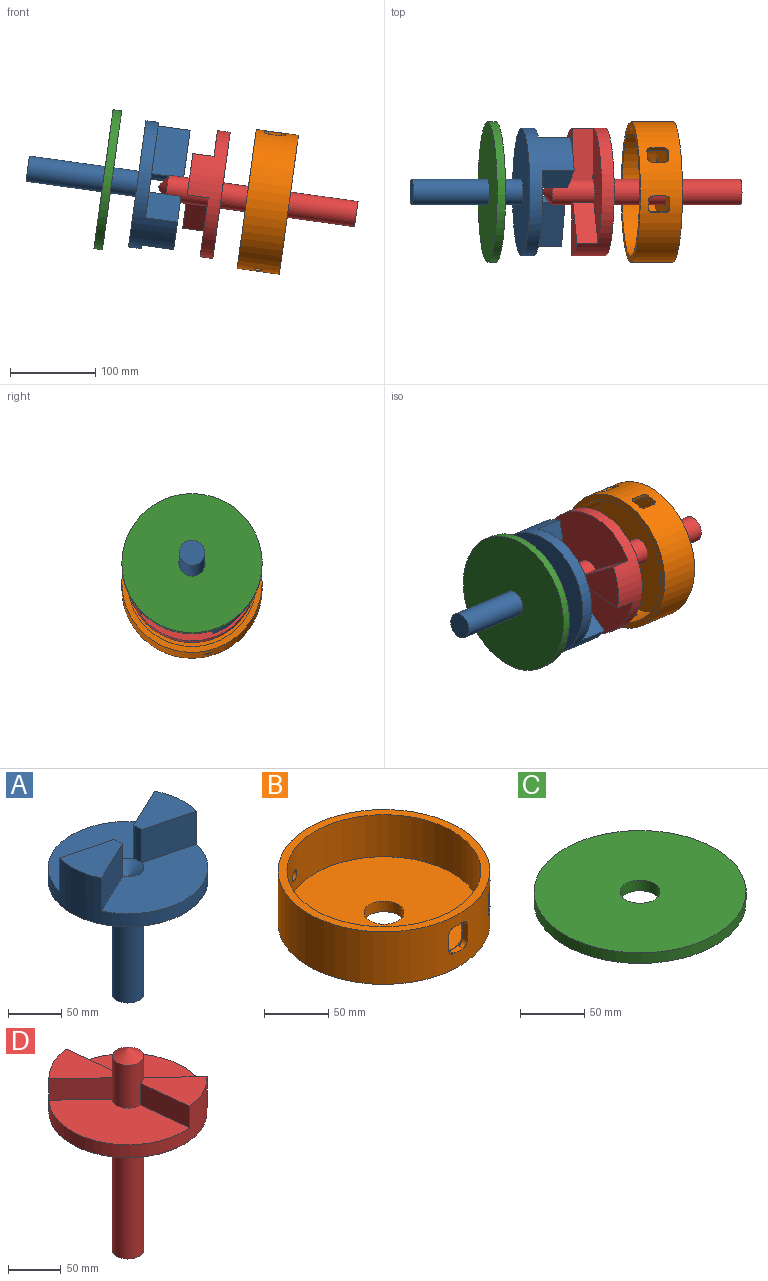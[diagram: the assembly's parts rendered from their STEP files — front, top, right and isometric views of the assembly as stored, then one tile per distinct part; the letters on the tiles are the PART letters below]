
ASSEMBLY  parts=4 mates=3
PART A: 14 faces, bbox 150x150x183 mm
  f0: plane 140.27x71.28mm, normal (0,0,1), area 6597.3mm2, adj f2,f6,f7,f9
  f1: plane 61.48x51.05mm, normal (0,0,1), area 1885mm2, adj f2,f4,f6,f9
  f2: cylinder r=75mm len=150mm, axis (0,0,-1), area 11047.9mm2, adj f0,f1,f3,f4,f5,f6,f7,f8
  f3: plane 61.48x51.05mm, normal (0,0,1), area 1885mm2, adj f2,f5,f7,f9
  f4: plane 54.09x38mm, normal (0.43,-0.9,0), area 2280mm2, adj f1,f2,f8,f9
  f5: plane 58.13x38mm, normal (-0.25,-0.97,0), area 2280mm2, adj f2,f3,f8,f9
  f6: plane 58.13x38mm, normal (0.25,0.97,0), area 2280mm2, adj f0,f1,f2,f9
  f7: plane 54.09x38mm, normal (-0.43,0.9,0), area 2280mm2, adj f0,f2,f3,f9
  f8: plane 140.27x71.28mm, normal (0,0,1), area 6597.3mm2, adj f2,f4,f5,f9
  f9: cylinder r=15mm len=38mm, axis (0,0,1), area 795.9mm2, adj f0,f1,f3,f4,f5,f6,f7,f8
  f10: plane 150x150mm, normal (0,0,-1), area 16964.6mm2, adj f2,f11
  f11: cylinder r=15mm len=130mm, axis (0,0,1), area 12252.2mm2, adj f10,f12
  f12: plane 30x30mm, normal (0,0,-1), area 706.9mm2, adj f11
  f13: cone r=15mm half-angle=56.3deg, axis (0,0,1), area 849.5mm2, adj f9
PART B: 40 faces, bbox 165x165x50 mm
  f0: cylinder r=75.5mm len=151mm, axis (0,0,-1), area 17629.2mm2, adj f2,f3,f14,f15,f16,f17,f18,f19
  f1: cylinder r=82.5mm len=165mm, axis (0,0,-1), area 24886mm2, adj f2,f4,f6,f7,f8,f9,f10,f11
  f2: plane 165x165mm, normal (0,0,1), area 3474.6mm2, adj f0,f1
  f3: plane 151x151mm, normal (0,0,1), area 17153.1mm2, adj f0,f5
  f4: plane 165x165mm, normal (0,0,-1), area 20627.7mm2, adj f1,f5
  f5: cylinder r=15.5mm len=31mm, axis (0,0,-1), area 973.9mm2, adj f3,f4
  f6: plane 10x5.19mm, normal (0,0,-1), area 50mm2, adj f1,f10,f13,f14
  f7: plane 15x5.34mm, normal (1,0,0), area 80.1mm2, adj f1,f10,f11,f18
  f8: plane 10x5.19mm, normal (0,0,1), area 50mm2, adj f1,f11,f12,f21
  f9: plane 15x5.31mm, normal (-1,0,0), area 79.7mm2, adj f1,f12,f13,f17
  f10: cylinder r=5mm len=5.82mm, axis (0,-1,0), area 40.8mm2, adj f1,f6,f7,f16
  f11: cylinder r=5mm len=5.82mm, axis (0,1,0), area 40.8mm2, adj f1,f7,f8,f20
  f12: cylinder r=5mm len=5.74mm, axis (0,-1,0), area 40.7mm2, adj f1,f8,f9,f19
  f13: cylinder r=5mm len=5.74mm, axis (0,1,0), area 40.7mm2, adj f1,f6,f9,f15
  f14: torus R=77.5mm, axis (0,0,-1), area 30.9mm2, adj f0,f6,f15,f16
  f15: bspline ~8.33x7.39mm, area 26.8mm2, adj f0,f13,f14,f17
  f16: bspline ~8.55x8.33mm, area 26.7mm2, adj f0,f10,f14,f18
  f17: cylinder r=2mm len=15mm, axis (0,0,-1), area 42.6mm2, adj f0,f9,f15,f19
  f18: cylinder r=2mm len=15mm, axis (0,0,-1), area 42.3mm2, adj f0,f7,f16,f20
  f19: bspline ~8.55x7.2mm, area 26.8mm2, adj f0,f12,f17,f21
  f20: bspline ~8.55x8.33mm, area 26.7mm2, adj f0,f11,f18,f21
  f21: torus R=77.5mm, axis (0,0,-1), area 30.9mm2, adj f0,f8,f19,f20
  f22: plane 15x3.88mm, normal (0.71,0.71,0), area 82.2mm2, adj f1,f26,f29,f30
  f23: plane 10.99x10.24mm, normal (0,0,-1), area 50.1mm2, adj f1,f26,f27,f33
  f24: plane 15x3.67mm, normal (-0.71,-0.71,0), area 77.8mm2, adj f1,f27,f28,f37
  f25: plane 10.99x10.24mm, normal (0,0,1), area 50.1mm2, adj f1,f28,f29,f34
  f26: cylinder r=5mm len=7.92mm, axis (-0.71,0.71,0), area 41.6mm2, adj f1,f22,f23,f31
  f27: cylinder r=5mm len=7.35mm, axis (0.71,-0.71,0), area 40.1mm2, adj f1,f23,f24,f35
  f28: cylinder r=5mm len=7.35mm, axis (-0.71,0.71,0), area 40.1mm2, adj f1,f24,f25,f36
  f29: cylinder r=5mm len=7.92mm, axis (0.71,-0.71,0), area 41.6mm2, adj f1,f22,f25,f32
  f30: cylinder r=2mm len=15mm, axis (0,0,-1), area 40.8mm2, adj f0,f22,f31,f32
  f31: bspline ~8.54x7.77mm, area 26.3mm2, adj f0,f26,f30,f33
  f32: bspline ~7.77x7.39mm, area 26.3mm2, adj f0,f29,f30,f34
  f33: torus R=77.5mm, axis (0,0,1), area 31mm2, adj f0,f23,f31,f35
  f34: torus R=77.5mm, axis (0,0,1), area 31mm2, adj f0,f25,f32,f36
  f35: bspline ~8.56x7.28mm, area 27.2mm2, adj f0,f27,f33,f37
  f36: bspline ~8.56x6.69mm, area 27.2mm2, adj f0,f28,f34,f37
  f37: cylinder r=2mm len=15mm, axis (0,0,-1), area 44.1mm2, adj f0,f24,f35,f36
  f38: cone r=5mm half-angle=5deg, axis (0.38,-0.92,0), area 75mm2, adj f1,f39
  f39: cone r=5mm half-angle=5deg, axis (-0.38,0.92,0), area 138.4mm2, adj f0,f38
PART C: 4 faces, bbox 165x165x10 mm
  f0: cylinder r=82.5mm len=165mm, axis (0,0,-1), area 5183.6mm2, adj f1,f2
  f1: plane 165x165mm, normal (0,0,1), area 20627.7mm2, adj f0,f3
  f2: plane 165x165mm, normal (0,0,-1), area 20627.7mm2, adj f0,f3
  f3: cylinder r=15.5mm len=31mm, axis (0,0,1), area 973.9mm2, adj f1,f2
PART D: 15 faces, bbox 150x150x235 mm
  f0: cylinder r=15mm len=160mm, axis (0,0,-1), area 15079.6mm2, adj f3,f12
  f1: plane 126.89x83.13mm, normal (0,0,1), area 6597.3mm2, adj f6,f8,f10,f11
  f2: plane 126.89x83.13mm, normal (0,0,1), area 6597.3mm2, adj f6,f7,f9,f11
  f3: plane 150x150mm, normal (0,0,-1), area 16964.6mm2, adj f0,f11
  f4: plane 64.18x52.52mm, normal (0,0,1), area 1885mm2, adj f6,f9,f10,f11
  f5: plane 64.18x52.52mm, normal (0,0,1), area 1885mm2, adj f6,f7,f8,f11
  f6: cylinder r=15mm len=50mm, axis (0,0,-1), area 4188.8mm2, adj f1,f2,f4,f5,f7,f8,f9,f10
  f7: plane 59.65x25mm, normal (-0.99,-0.11,0), area 1500mm2, adj f2,f5,f6,f11
  f8: plane 43.32x41.51mm, normal (0.69,0.72,0), area 1500mm2, adj f1,f5,f6,f11
  f9: plane 43.32x41.51mm, normal (-0.69,-0.72,0), area 1500mm2, adj f2,f4,f6,f11
  f10: plane 59.65x25mm, normal (0.99,0.11,0), area 1500mm2, adj f1,f4,f6,f11
  f11: cylinder r=75mm len=150mm, axis (0,0,-1), area 9686.6mm2, adj f1,f2,f3,f4,f5,f7,f8,f9
  f12: plane 30x30mm, normal (0,0,-1), area 706.9mm2, adj f0
  f13: cone r=15mm half-angle=56.3deg, axis (0,0,-1), area 849.6mm2, adj f6,f14
  f14: plane 0.01x0.01mm, normal (0,0,1), area 0mm2, adj f13
PLACE A rot(axis=(-0.36,0.88,-0.32),105.3deg) t=(-80.97,68.63,-91.55)mm
PLACE B rot(axis=(-0.52,-0.62,0.59),109.4deg) t=(77.52,68.63,-113.45)mm
PLACE C rot(axis=(0.35,-0.85,-0.4),91.7deg) t=(-120.59,68.63,-86.07)mm
PLACE D rot(axis=(-0.66,-0.06,0.75),172.5deg) t=(-6.68,68.63,-101.82)mm
MATE revolute D.f0 <-> A.f9  axis (0.99,0,-0.14) through (-56.21,68.63,-94.97)mm
MATE fastened B.f5 <-> D.f11  axis (-0.99,0,0.14) through (77.52,68.63,-113.45)mm
MATE fastened C.f3 <-> A.f11  axis (0.99,0,-0.14) through (-120.59,68.63,-86.07)mm
